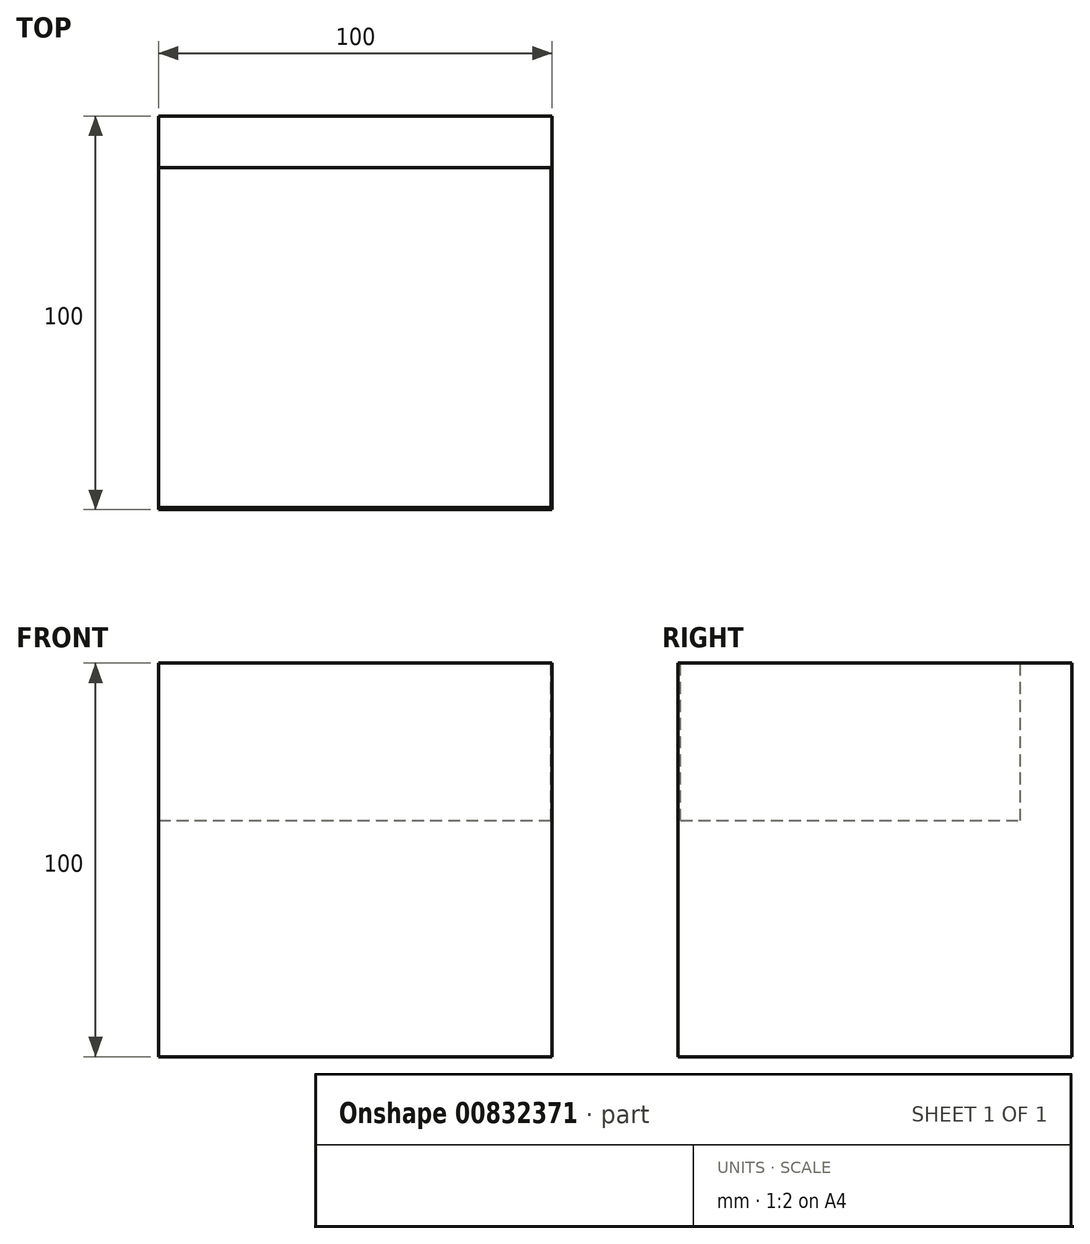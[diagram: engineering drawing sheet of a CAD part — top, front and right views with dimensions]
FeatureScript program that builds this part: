
annotation { "Feature Type Name" : "Feature", "Feature Type Description" : "" }
export const myFeature = defineFeature(function(context is Context, id is Id, definition is map)
    precondition{}
    {
        {
            var Q0;
            Q0=qCreatedBy(makeId("Top.planeOp"),FACE);
            var sketch = newSketch(context, id + "F0", { "sketchPlane" : qUnion([Q0])});
            skLineSegment(sketch, "E0.bottom", {"start": v(-50, -50) * mm, "end": v(50, -50) * mm});
            skLineSegment(sketch, "E0.top", {"start": v(-50, 50) * mm, "end": v(50, 50) * mm});
            skLineSegment(sketch, "E0.left", {"start": v(-50, -50) * mm, "end": v(-50, 50) * mm});
            skLineSegment(sketch, "E0.right", {"start": v(50, -50) * mm, "end": v(50, 50) * mm});
            skPoint(sketch, "E0.middle", {"position": v(0, 0) * mm});
            skSolve(sketch);
        }
        {
            var Q0;
            Q0 = qSketchRegion(id + "F0", true);
            extrude(context, id + "F1", {"entities" : qUnion([Q0]), "depth" : 100 * mm, "offsetDistance" : 25 * mm});
        }
        {
            var Q0;
            Q0=makeQuery(id+"F1.opExtrude","CAP_FACE",FACE,{"disambiguationData":[OSD([sQuery(id+"F0.wireOp",EDGE,"E0.bottom"),sQuery(id+"F0.wireOp",EDGE,"E0.top"),sQuery(id+"F0.wireOp",EDGE,"E0.left"),sQuery(id+"F0.wireOp",EDGE,"E0.right")])],"isStart":false});
            var sketch = newSketch(context, id + "F2", { "sketchPlane" : qUnion([Q0])});
            skSolve(sketch);
        }
        {
            var Q0;
            Q0=makeQuery(id+"F2.imprint","IMPRINT",FACE,{"disambiguationData":[TD([[makeQuery(id+"F2.imprint","IMPRINT",EDGE,{"derivedFrom":makeQuery(id+"F1.opExtrude","CAP_EDGE",EDGE,{"disambiguationData":[OSD([sQuery(id+"F0.wireOp",EDGE,"E0.bottom")])],"isStart":false})}),1.0]])]});
            var sketch = newSketch(context, id + "F3", { "sketchPlane" : qUnion([Q0])});
            skLineSegment(sketch, "E1.bottom", {"start": v(-50.37, -49.43) * mm, "end": v(49.66, -49.43) * mm});
            skLineSegment(sketch, "E1.top", {"start": v(-50.37, 36.95) * mm, "end": v(49.66, 36.95) * mm});
            skLineSegment(sketch, "E1.left", {"start": v(-50.37, -49.43) * mm, "end": v(-50.37, 36.95) * mm});
            skLineSegment(sketch, "E1.right", {"start": v(49.66, -49.43) * mm, "end": v(49.66, 36.95) * mm});
            skSolve(sketch);
        }
        {
            var Q0;
            Q0 = qSketchRegion(id + "F3", true);
            extrude(context, id + "F4", {"entities" : qUnion([Q0]), "operationType" : NewBodyOperationType.REMOVE, "oppositeDirection" : true, "depth" : 40 * mm, "offsetDistance" : 25 * mm});
        }
    });
